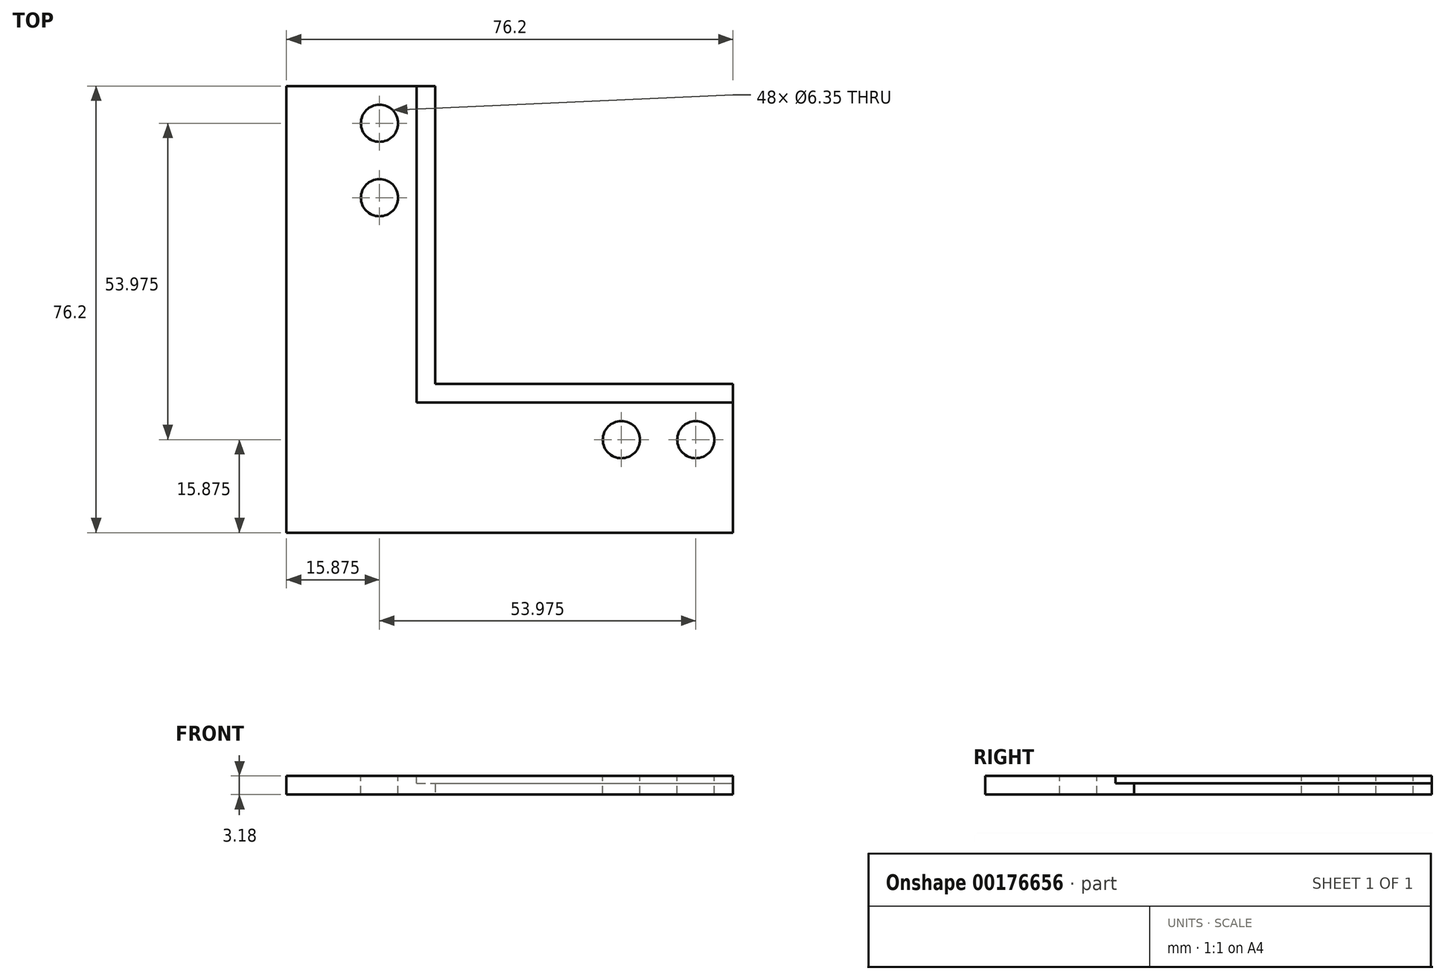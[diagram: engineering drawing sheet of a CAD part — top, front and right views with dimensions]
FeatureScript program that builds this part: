
annotation { "Feature Type Name" : "Feature", "Feature Type Description" : "" }
export const myFeature = defineFeature(function(context is Context, id is Id, definition is map)
    precondition{}
    {
        {
            var Q0;
            Q0=qCreatedBy(makeId("Top.planeOp"),FACE);
            var sketch = newSketch(context, id + "F0", { "sketchPlane" : qUnion([Q0])});
            skLineSegment(sketch, "E0.bottom", {"start": v(0, 0) * mm, "end": v(76.2, 0) * mm});
            skLineSegment(sketch, "E0.top", {"start": v(0, 76.2) * mm, "end": v(25.4, 76.2) * mm});
            skLineSegment(sketch, "E0.left", {"start": v(0, 0) * mm, "end": v(0, 76.2) * mm});
            skLineSegment(sketch, "E0.right", {"start": v(76.2, 0) * mm, "end": v(76.2, 25.4) * mm});
            skLineSegment(sketch, "E1.top", {"start": v(25.4, 25.4) * mm, "end": v(76.2, 25.4) * mm});
            skLineSegment(sketch, "E1.left", {"start": v(25.4, 76.2) * mm, "end": v(25.4, 25.4) * mm});
            skSolve(sketch);
        }
        {
            var Q0;
            Q0 = qSketchRegion(id + "F0", true);
            extrude(context, id + "F1", {"entities" : qUnion([Q0]), "depth" : 3.17 * mm});
        }
        {
            var Q0;
            Q0=makeQuery(id+"F1.opExtrude","CAP_FACE",FACE,{"disambiguationData":[OSD([sQuery(id+"F0.wireOp",EDGE,"E0.bottom"),sQuery(id+"F0.wireOp",EDGE,"E0.top"),sQuery(id+"F0.wireOp",EDGE,"E0.left"),sQuery(id+"F0.wireOp",EDGE,"E0.right"),sQuery(id+"F0.wireOp",EDGE,"E1.top"),sQuery(id+"F0.wireOp",EDGE,"E1.left")])],"isStart":false});
            var sketch = newSketch(context, id + "F2", { "sketchPlane" : qUnion([Q0])});
            skLineSegment(sketch, "E2.top", {"start": v(25.4, 76.2) * mm, "end": v(22.22, 76.2) * mm});
            skLineSegment(sketch, "E2.left", {"start": v(25.4, 25.4) * mm, "end": v(25.4, 76.2) * mm});
            skLineSegment(sketch, "E2.right", {"start": v(22.23, 25.4) * mm, "end": v(22.22, 76.2) * mm});
            skLineSegment(sketch, "E3.bottom", {"start": v(25.4, 25.4) * mm, "end": v(76.2, 25.4) * mm});
            skLineSegment(sketch, "E3.top", {"start": v(25.4, 22.23) * mm, "end": v(76.2, 22.23) * mm});
            skLineSegment(sketch, "E3.right", {"start": v(76.2, 25.4) * mm, "end": v(76.2, 22.23) * mm});
            skLineSegment(sketch, "E4.top", {"start": v(22.23, 22.23) * mm, "end": v(25.4, 22.23) * mm});
            skLineSegment(sketch, "E4.left", {"start": v(22.23, 25.4) * mm, "end": v(22.23, 22.23) * mm});
            skSolve(sketch);
        }
        {
            var Q0;
            Q0 = qSketchRegion(id + "F2", true);
            extrude(context, id + "F3", {"entities" : qUnion([Q0]), "operationType" : NewBodyOperationType.REMOVE, "oppositeDirection" : true, "depth" : 1.27 * mm});
        }
        {
            var Q0;
            Q0=makeQuery(id+"F1.opExtrude","CAP_FACE",FACE,{"disambiguationData":[OSD([sQuery(id+"F0.wireOp",EDGE,"E0.bottom"),sQuery(id+"F0.wireOp",EDGE,"E0.top"),sQuery(id+"F0.wireOp",EDGE,"E0.left"),sQuery(id+"F0.wireOp",EDGE,"E0.right"),sQuery(id+"F0.wireOp",EDGE,"E1.top"),sQuery(id+"F0.wireOp",EDGE,"E1.left")])],"isStart":false});
            var sketch = newSketch(context, id + "F4", { "sketchPlane" : qUnion([Q0])});
            skCircle(sketch, "E5", {"center": v(69.85, 15.88) * mm, "radius": 3.18 * mm});
            skCircle(sketch, "E6", {"center": v(57.15, 15.88) * mm, "radius": 3.18 * mm});
            skCircle(sketch, "E7", {"center": v(15.88, 69.85) * mm, "radius": 3.18 * mm});
            skCircle(sketch, "E8", {"center": v(15.88, 57.15) * mm, "radius": 3.18 * mm});
            skSolve(sketch);
        }
        {
            var Q0;
            Q0 = qSketchRegion(id + "F4", true);
            extrude(context, id + "F5", {"entities" : qUnion([Q0]), "operationType" : NewBodyOperationType.REMOVE, "oppositeDirection" : true, "depth" : 25.4 * mm});
        }
    });
